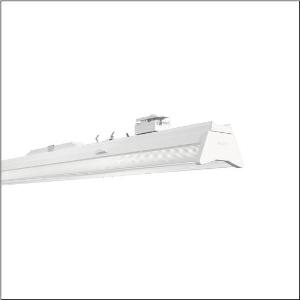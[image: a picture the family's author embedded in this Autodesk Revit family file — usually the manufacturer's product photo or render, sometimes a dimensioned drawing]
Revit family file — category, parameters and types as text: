
# Revit family: licross_r__11_performance_mo_51td16mn4axg_aad5
name_source: partatom
category: Lighting Fixtures
units: mm (PartAtom-declared; Revit-internal decimal feet)

## family parameters
Cut with Voids When Loaded = No
Host = Face
Light Source = No
Part Type = Normal
Room Calculation Point = No
Round Connector Dimension = Use Diameter
Shared = No

## types (1)
- --- (1 x LED, 10160 lm, 55.3 W, 4000K)
    Apparent Load = 55 VA
    CIE Flux Codes = 66 88 96 79 100
    Color Rendering = 80
    Color Temperature = 4000K
    Default Elevation = 1800 mm
    Description = Licross® 11 Performance MO, luminaire insert, of sheet steel, galvanised, coil coated, white, length: 1.500mm, width: 120mm, height: 123mm, LED rated luminous flux: 10.160lm, light colour: 840, SDCM (Standard Deviation of Colour Matching)MacAdam ≤ 2 SDCM (initial), control gear: ON/OFF Multilumen, with plug, 3-pole, with phase selection, mains connection: 220..240V, AC, 50/60Hz, rated input power: 55W, internal wiring halogen-free, primary light control with lens, of plastic, primary optical cover: cover, of PMMA, light emission: direct/indirect distribution, primary light characteristic: symmetric, protection rating (complete): IP54, insulation class (complete): insulation class I (protective earthing), certification: CE, ENEC, VDE, UKCA, protection symbol: D if used in an environment with non-conductive dust loads with corresponding accessories, impact resistance: IK06, permissible ambient temperature for indoor applications: -35..+40°C, corresponds to IFS (International Featured Standards) requirements for safety and quality in the food industry, reducing of maximum allowable ambient temperature of 5°C with ceiling mounting, LABS conformity tested according to VDMA 24364:2018-05, packaging unit: 1 piece
    Height = 114 mm
    Lamp = 1 x LED
    Lamp Light Flux = 10160 lm
    Lamp Power = 55.3 W
    Lamp count = 1
    Length = 1500 mm
    Luminous efficacy = 184 lm/W
    Manufacturer = Siteco
    ModVariant = No
    Model = 51TD16MN4AXG
    Mounting Place = Ceiling
    Mounting Type = Pendant
    Number of Poles = 1
    OnlyDefault = Yes
    Power Factor = 1
    Product Name = Licross® 11 Performance MO
    Product group = luminaire insert | ceiling pendant
    ProductGroupID = 901
    Protection Class = Protection class I
    Protection Degree = IP 54
    RLX_Detail_Level = 1
    RLX_Emergency_Light_Flux = 0 lm
    RLX_Emergency_Type = 0
    RLX_Emergency_Type_DB = No
    RlxData = <blob elided: 31953 chars, md5=c58e91b1>
    Socket = socket
    Standby Power = 0 W
    System Light Flux = 10160 lm
    System Power = 55 W
    Type Comments = factory setting: luminous flux: 100 % | (A | C | E) | 126 mA
    Type Image = l_1256138.jpg
    URL = http://relux.com
    VarID = @adj_093827
    Voltage = 0 V
    Weight = 0.00 kg
    Width = 120 mm

## geometry (parser evidence)
native form markers: Blend x4, Sweep x13
no freeform markers — native parametric forms only
